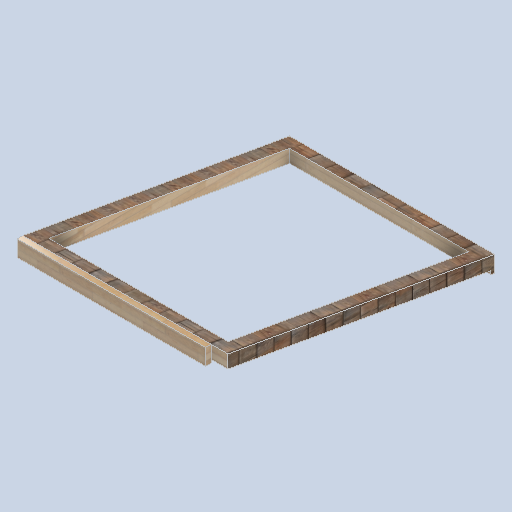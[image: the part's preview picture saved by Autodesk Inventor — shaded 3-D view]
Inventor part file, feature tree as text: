
AUTODESK INVENTOR PART (.ipt)
format: ipt  version: 2024.2 (Build 282272000, 272)  size: 186,880 bytes
history: native  units: in
note: dims shown in document units (in); Inventor stores cm internally (conversion verified against a paired STEP export)
features: sketch x7, plane x5, other x3
ambient origin geometry x8: Origin, YZ Plane, XZ Plane, XY Plane, X Axis, Y Axis, Z Axis, Center Point
bodies: Solid1 (feature_tree)
feature tree (15):
  other  "eave_frame_02.ipt"
  other  "Solid1::eave_frame_02.ipt"
  other  "TaggingFeature1"
  sketch  "Sketch3"  dims[d0=0.3937in]
  sketch  "Sketch4"
  sketch  "Sketch5"
  sketch  "Sketch6"
  sketch  "Sketch7"
  sketch  "Sketch8"
  sketch  "Sketch9"
  plane  "Work Plane1"
  plane  "Work Plane2"
  plane  "Work Plane3"
  plane  "Work Plane4"
  plane  "Work Plane5"
